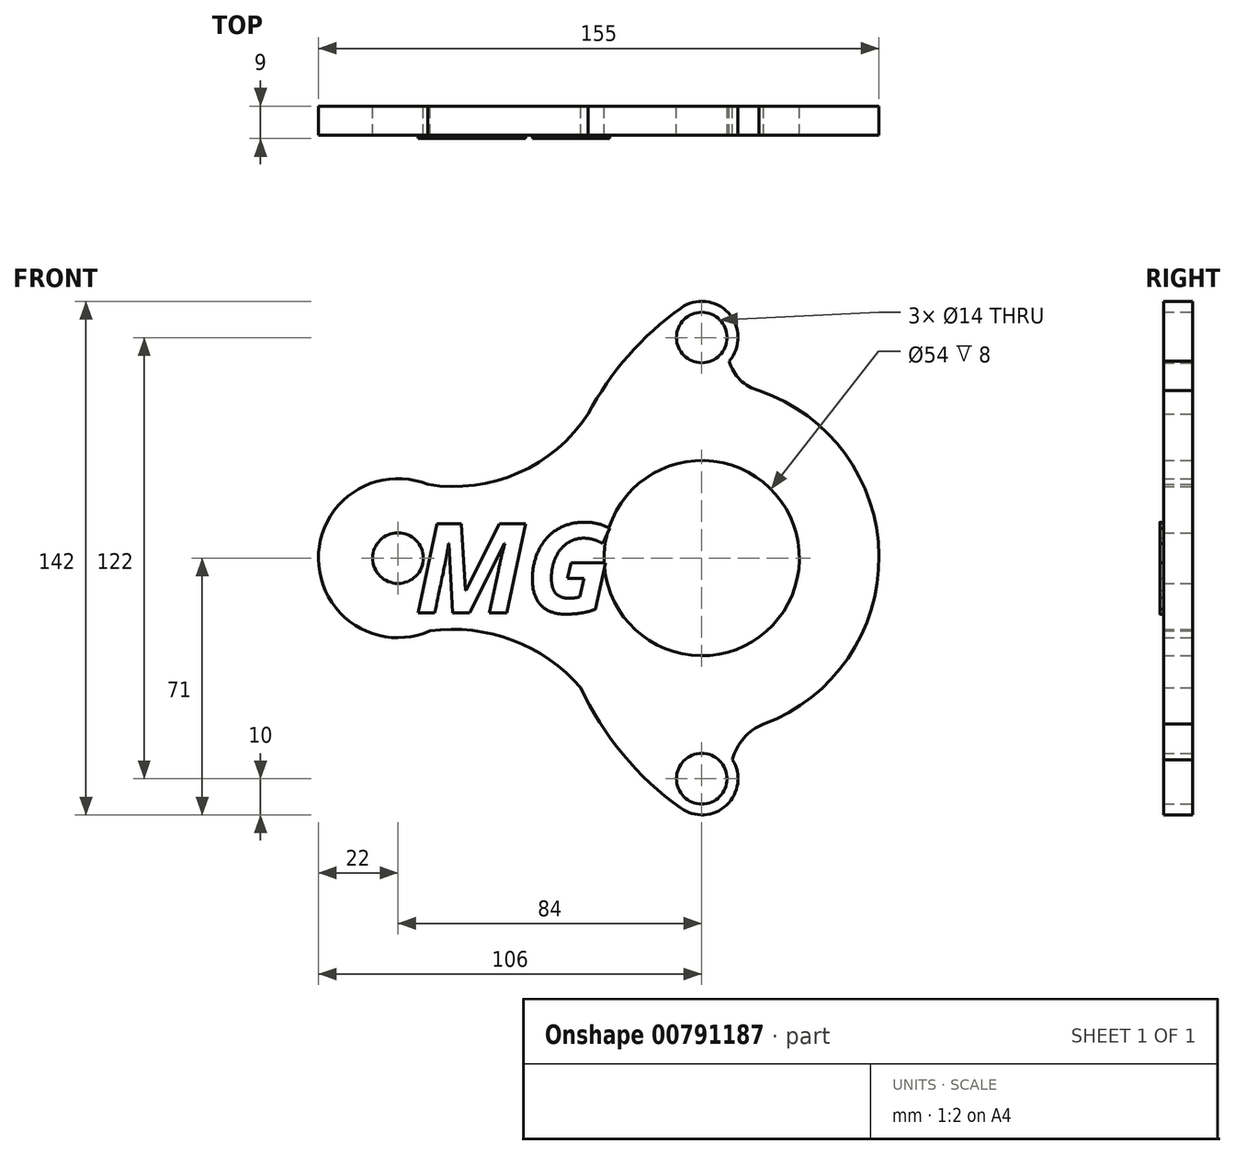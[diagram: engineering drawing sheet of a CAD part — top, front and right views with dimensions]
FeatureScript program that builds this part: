
annotation { "Feature Type Name" : "Feature", "Feature Type Description" : "" }
export const myFeature = defineFeature(function(context is Context, id is Id, definition is map)
    precondition{}
    {
        {
            var Q0;
            Q0=qCreatedBy(makeId("Front.planeOp"),FACE);
            var sketch = newSketch(context, id + "F0", { "sketchPlane" : qUnion([Q0])});
            skCircle(sketch, "E0", {"center": v(0, 0) * mm, "radius": 27 * mm});
            skLineSegment(sketch, "E1", {"start": v(0, 0) * mm, "end": v(-84, 0) * mm});
            skLineSegment(sketch, "E2", {"start": v(0, 0) * mm, "end": v(0, 61) * mm});
            skLineSegment(sketch, "E3", {"start": v(0, 0) * mm, "end": v(0, -61) * mm});
            skCircle(sketch, "E4", {"center": v(0, 61) * mm, "radius": 7 * mm});
            skCircle(sketch, "E5", {"center": v(0, 61) * mm, "radius": 10 * mm});
            skCircle(sketch, "E6", {"center": v(0, -61) * mm, "radius": 7 * mm});
            skCircle(sketch, "E7", {"center": v(0, -61) * mm, "radius": 10 * mm});
            skCircle(sketch, "E8", {"center": v(-84, 0) * mm, "radius": 7 * mm});
            skArc(sketch, "E9", {"start": v(-75.76, 20.4) * mm, "mid": v(-106, -0.34) * mm, "end": v(-75.14, -20.14) * mm});
            skArc(sketch, "E10", {"start": v(-5.82, 69.13) * mm, "mid": v(-20.3, 56) * mm, "end": v(-31.4, 39.92) * mm});
            skArc(sketch, "E11", {"start": v(-75.76, 20.4) * mm, "mid": v(-50.67, 23.55) * mm, "end": v(-31.4, 39.92) * mm});
            skArc(sketch, "E12", {"start": v(-33.46, -35.8) * mm, "mid": v(-52.32, -22.7) * mm, "end": v(-75.14, -20.14) * mm});
            skArc(sketch, "E13", {"start": v(17.1, -45.92) * mm, "mid": v(11.6, -49.77) * mm, "end": v(8.5, -55.73) * mm});
            skArc(sketch, "E14", {"start": v(7.59, 54.49) * mm, "mid": v(10.61, 49.32) * mm, "end": v(15.83, 46.37) * mm});
            skArc(sketch, "E15.trimOffspring", {"start": v(-36.89, -32.26) * mm, "mid": v(-35.22, -34.07) * mm, "end": v(-33.46, -35.8) * mm});
            skArc(sketch, "E16.trimOffspring", {"start": v(-33.46, -35.8) * mm, "mid": v(-21.8, -54.26) * mm, "end": v(-5.82, -69.13) * mm});
            skArc(sketch, "E17.trimOffspring", {"start": v(17.1, -45.92) * mm, "mid": v(48.98, 1.4) * mm, "end": v(14.43, 46.83) * mm});
            skSolve(sketch);
        }
        {
            var Q0;
            Q0=makeQuery(id+"F0.imprint","IMPRINT",FACE,{"disambiguationData":[TD([[makeQuery(id+"F0.imprint","IMPRINT",EDGE,{"derivedFrom":sQuery(id+"F0.wireOp",EDGE,"E8")}),-1.0]])]});
            var Q1;
            {var subQ8=sQuery(id+"F0.wireOp",EDGE,"E13");Q1=makeQuery(id+"F0.imprint","IMPRINT",FACE,{"disambiguationData":[TD([[makeQuery(id+"F0.imprint","IMPRINT",EDGE,{"derivedFrom":subQ8}),-1.0]])]});}
            var Q2;
            Q2=makeQuery(id+"F0.imprint","IMPRINT",FACE,{"disambiguationData":[TD([[makeQuery(id+"F0.imprint","IMPRINT",EDGE,{"derivedFrom":sQuery(id+"F0.wireOp",EDGE,"E6")}),-1.0]])]});
            var Q3;
            Q3=makeQuery(id+"F0.imprint","IMPRINT",FACE,{"disambiguationData":[TD([[makeQuery(id+"F0.imprint","IMPRINT",EDGE,{"derivedFrom":sQuery(id+"F0.wireOp",EDGE,"E4")}),-1.0]])]});
            extrude(context, id + "F1", {"entities" : qUnion([Q0, Q1, Q2, Q3]), "depth" : 8 * mm, "offsetDistance" : 25 * mm});
        }
        {
            var Q0;
            Q0=makeQuery(id+"F1.opExtrude","CAP_FACE",FACE,{"disambiguationData":[OSD([sQuery(id+"F0.wireOp",EDGE,"E0"),sQuery(id+"F0.wireOp",EDGE,"E4"),sQuery(id+"F0.wireOp",EDGE,"E5"),sQuery(id+"F0.wireOp",EDGE,"E6"),sQuery(id+"F0.wireOp",EDGE,"E7"),sQuery(id+"F0.wireOp",EDGE,"E8"),sQuery(id+"F0.wireOp",EDGE,"E9"),sQuery(id+"F0.wireOp",EDGE,"E10"),sQuery(id+"F0.wireOp",EDGE,"E11"),sQuery(id+"F0.wireOp",EDGE,"E12"),sQuery(id+"F0.wireOp",EDGE,"E13"),sQuery(id+"F0.wireOp",EDGE,"E14"),sQuery(id+"F0.wireOp",EDGE,"E16.trimOffspring"),sQuery(id+"F0.wireOp",EDGE,"E17.trimOffspring")])],"isStart":false});
            var sketch = newSketch(context, id + "F2", { "sketchPlane" : qUnion([Q0])});
            skText(sketch, "E18", { "text": "MG", "fontName": "OpenSans-BoldItalic.ttf"});
            const initialGuessF2  = {"E18": [-0.07938, -0.01516, 1, 0, 0.02493]};
            skSetInitialGuess(sketch, initialGuessF2);
            skSolve(sketch);
        }
        {
            var Q0;
            Q0 = qSketchRegion(id + "F2", true);
            extrude(context, id + "F3", {"entities" : qUnion([Q0]), "operationType" : NewBodyOperationType.ADD, "depth" : 1 * mm, "offsetDistance" : 25 * mm});
        }
    });
